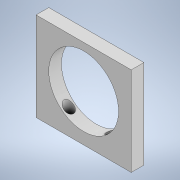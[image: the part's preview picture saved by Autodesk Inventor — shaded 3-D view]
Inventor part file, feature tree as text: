
AUTODESK INVENTOR PART (.ipt)
format: ipt  version: 2022 (Build 260153000, 153)  size: 126,464 bytes
history: native  units: mm
features: sketch x3, extrude x2, hole x1
ambient origin geometry x8: Origin, YZ Plane, XZ Plane, XY Plane, X Axis, Y Axis, Z Axis, Center Point
bodies: Solid1 (feature_tree)
feature tree (6):
  extrude  "Extrusion1"  Depth=6.0mm
  hole  "Hole1"  [1 undecoded]
  extrude  "Extrusion3"  Depth=10.0mm
  sketch  "Sketch1"  dims[d0=45.0mm d1=6.0mm]
  sketch  "Sketch3"  dims[d2=42.0mm d3=0.0mm d9=3.0mm]
  sketch  "Sketch4"  dims[d10=10.0mm d11=10.0mm d12=4.5mm d13=6.0mm d14=5.0mm d15=2.0mm d16=90.0deg d17=11.0mm d18=20.594885mm d19=22.0mm d20=33.0mm d21=0.0mm d22=0.0mm]
note: 1 required parameter value undecoded (feature->parameter linkage not recoverable at this tier; creation-order binding heuristic only, values carry confidence <= 0.55)
